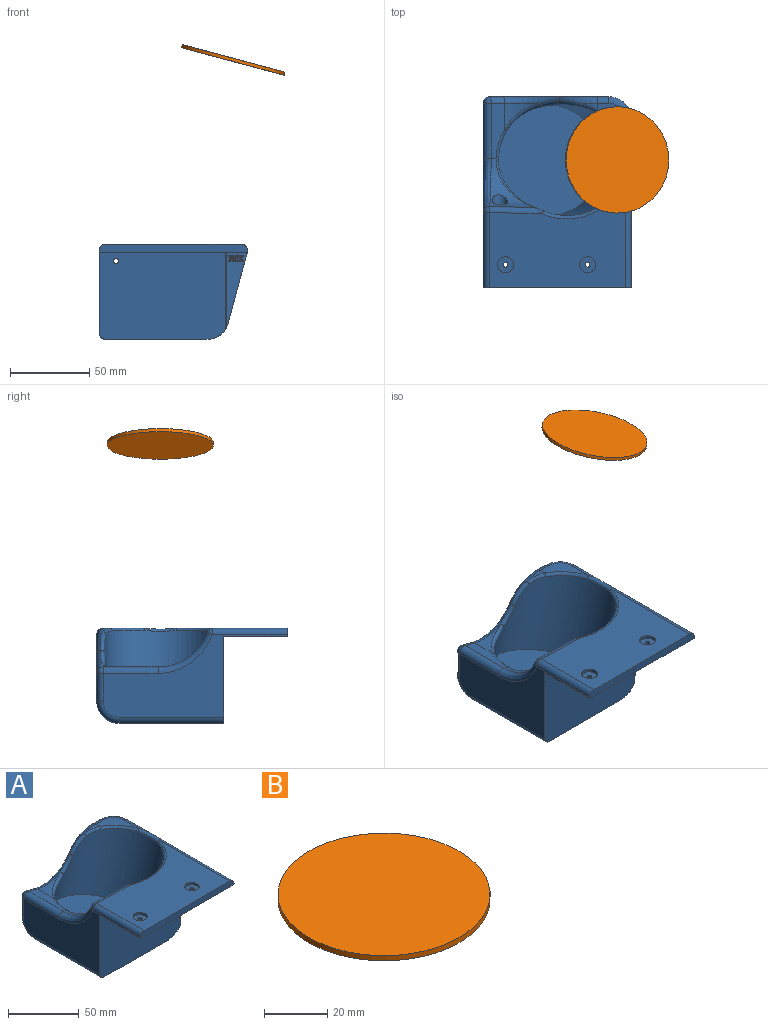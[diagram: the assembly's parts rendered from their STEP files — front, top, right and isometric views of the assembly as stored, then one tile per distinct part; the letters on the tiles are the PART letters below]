
ASSEMBLY  parts=2 mates=1
PART A: 290 faces, bbox 113.1x121.2x77.5 mm
  f0: plane 85.53x69.51mm, normal (0,0,1), area 3915.7mm2, adj f6,f20,f23,f265,f269,f278,f284
  f1: plane 48x13.37mm, normal (0.55,-0.83,0), area 362.4mm2, adj f110,f112,f113,f116,f117,f118,f119,f120
  f2: plane 79.97x54.9mm, normal (0,-1,0), area 4355.7mm2, adj f4,f8,f15,f109,f110,f264,f276
  f3: plane 75.17x42mm, normal (0,1,0), area 1714.4mm2, adj f25,f262,f267,f268,f270,f272,f275
  f4: plane 66x63.92mm, normal (0,0,-1), area 4218.6mm2, adj f2,f262,f264,f276
  f5: plane 25.51x17.47mm, normal (0,0,1), area 186.1mm2, adj f14,f265,f266,f267,f280
  f6: plane 93.52x5mm, normal (0,-1,0), area 460.7mm2, adj f0,f7,f8,f115,f265,f269
  f7: plane 93.32x48.76mm, normal (0,0,-1), area 3768.2mm2, adj f6,f8,f18,f21,f109,f111,f113,f115
  f8: plane 116x52.01mm, normal (-1,0,0), area 2518.3mm2, adj f2,f6,f7,f109,f269,f271,f273,f275
  f9: plane 70x67.62mm, normal (0.26,0,0.97), area 3848.5mm2, adj f10
  f10: cylinder r=35mm len=82.02mm, axis (0.26,0,0.97), area 7874.1mm2, adj f9,f280,f281,f282,f283,f284,f285,f286
  f11: plane 64.98x44.59mm, normal (0.97,0,-0.26), area 2815.9mm2, adj f25,f112,f114,f264,f265
  f12: plane 34.64x8.58mm, normal (0.26,0,0.97), area 240.8mm2, adj f13,f24,f272,f273,f289
  f13: cylinder r=30mm len=23.04mm, axis (0,-1,0), area 196.4mm2, adj f12,f270,f287
  f14: cylinder r=30mm len=11.81mm, axis (0,-1,0), area 24.4mm2, adj f5,f268,f281
  f15: cylinder r=1.5mm len=8mm, axis (0,1,0), area 75.4mm2, adj f2,f16
  f16: plane 10x10mm, normal (0,1,0), area 71.5mm2, adj f15,f17
  f17: cylinder r=5mm len=10mm, axis (0,1,0), area 215.5mm2, adj f16,f24
  f18: cylinder r=1.5mm len=3mm, axis (0,0,1), area 28.3mm2, adj f7,f19
  f19: plane 10x10mm, normal (0,0,1), area 71.5mm2, adj f18,f20
  f20: cylinder r=5mm len=10mm, axis (0,0,1), area 62.8mm2, adj f0,f19
  f21: cylinder r=1.5mm len=3mm, axis (0,0,1), area 28.3mm2, adj f7,f22
  f22: plane 10x10mm, normal (0,0,1), area 71.5mm2, adj f21,f23
  f23: cylinder r=5mm len=10mm, axis (0,0,1), area 62.8mm2, adj f0,f22
  f24: bspline ~58.91x32.85mm, area 466mm2, adj f12,f17,f271,f278,f288
  f25: cylinder r=14mm len=48.21mm, axis (-0.26,0,-0.97), area 985.7mm2, adj f3,f11,f263,f266
  f26: extruded ~0.82x0.61mm, area 0.6mm2, adj f27,f53,f108,f260
  f27: plane 0.75x0.5mm, normal (-0.83,-0.55,0), area 0.1mm2, adj f26,f28,f108,f261
  f28: extruded ~0.82x0.67mm, area 0.6mm2, adj f27,f29,f108,f259
  f29: extruded ~0.98x0.85mm, area 0.5mm2, adj f28,f30,f108,f257
  f30: extruded ~0.91x0.75mm, area 0.3mm2, adj f29,f31,f108,f255
  f31: extruded ~0.86x0.67mm, area 0.3mm2, adj f30,f32,f108,f253
  f32: plane 1.25x0.75mm, normal (0.83,0.55,0), area 1.1mm2, adj f31,f33,f108,f252
  f33: extruded ~0.87x0.67mm, area 0.3mm2, adj f32,f34,f108,f254
  f34: extruded ~0.92x0.75mm, area 0.3mm2, adj f33,f53,f108,f256
  f35: extruded ~0.85x0.72mm, area 0.4mm2, adj f36,f52,f232,f250
  f36: plane 0.7x0.49mm, normal (0.82,0.55,0.16), area 0.3mm2, adj f35,f37,f233,f251
  f37: plane 1.33x1.26mm, normal (0,0,1), area 0.9mm2, adj f36,f38,f231,f249
  f38: plane 0.67x0.48mm, normal (-0.83,-0.55,0), area 0.4mm2, adj f37,f39,f229,f247
  f39: plane 0.88x0.76mm, normal (-0.17,-0.12,-0.98), area 0.3mm2, adj f38,f40,f227,f245
  f40: plane 3.68x0.67mm, normal (-0.83,-0.55,0), area 2.9mm2, adj f39,f41,f225,f243
  f41: plane 1.46x1.34mm, normal (0,0,-1), area 1mm2, adj f40,f42,f223,f241
  f42: plane 0.67x0.48mm, normal (0.83,0.55,0), area 0.4mm2, adj f41,f43,f221,f239
  f43: plane 0.9x0.8mm, normal (0.16,0.1,0.98), area 0.3mm2, adj f42,f44,f219,f237
  f44: plane 1.05x0.67mm, normal (0.83,0.55,0), area 0.8mm2, adj f43,f45,f217,f235
  f45: extruded ~0.84x0.7mm, area 0.3mm2, adj f44,f46,f216,f234
  f46: extruded ~0.89x0.77mm, area 0.3mm2, adj f45,f47,f218,f236
  f47: extruded ~1.15x1.14mm, area 0.8mm2, adj f46,f48,f220,f238
  f48: extruded ~1.12x0.83mm, area 0.9mm2, adj f47,f49,f222,f240
  f49: plane 0.67x0.44mm, normal (0.83,0.55,0), area 0mm2, adj f48,f50,f224,f242
  f50: extruded ~1.05x0.83mm, area 0.9mm2, adj f49,f51,f226,f244
  f51: extruded ~1.14x1.13mm, area 0.8mm2, adj f50,f52,f228,f246
  f52: extruded ~0.9x0.8mm, area 0.4mm2, adj f35,f51,f230,f248
  f53: extruded ~0.98x0.85mm, area 0.5mm2, adj f26,f34,f108,f258
  f54: plane 4.09x2.35mm, normal (0.55,-0.83,0), area 4.9mm2, adj f234,f235,f236,f237,f238,f239,f240,f241
  f55: plane 0.67x0.48mm, normal (-0.83,-0.55,0), area 0.4mm2, adj f56,f76,f189,f211
  f56: plane 1.8x1.57mm, normal (0,0,-1), area 1.3mm2, adj f55,f57,f187,f209
  f57: plane 0.67x0.48mm, normal (0.83,0.55,0), area 0.4mm2, adj f56,f58,f185,f207
  f58: plane 0.9x0.8mm, normal (0.16,0.11,0.98), area 0.3mm2, adj f57,f59,f183,f205
  f59: plane 2.1x0.67mm, normal (0.83,0.55,0), area 1.7mm2, adj f58,f60,f181,f203
  f60: plane 0.7x0.47mm, normal (0.13,0.09,-0.99), area 0mm2, adj f59,f61,f179,f181,f201
  f61: plane 2.66x1.77mm, normal (-0.71,-0.48,-0.51), area 2.5mm2, adj f60,f62,f179,f199
  f62: plane 1.45x1.34mm, normal (0,0,-1), area 1mm2, adj f61,f63,f177,f197
  f63: plane 0.67x0.48mm, normal (0.83,0.55,0), area 0.4mm2, adj f62,f64,f175,f195
  f64: plane 0.9x0.79mm, normal (0.16,0.11,0.98), area 0.3mm2, adj f63,f65,f174,f194
  f65: plane 2.83x0.67mm, normal (0.83,0.55,0), area 2.3mm2, adj f64,f66,f176,f196
  f66: plane 0.9x0.79mm, normal (0.16,0.11,-0.98), area 0.3mm2, adj f65,f67,f178,f198
  f67: plane 0.67x0.48mm, normal (0.83,0.55,0), area 0.4mm2, adj f66,f68,f180,f200
  f68: plane 1.8x1.57mm, normal (0,0,1), area 1.3mm2, adj f67,f69,f182,f202
  f69: plane 0.67x0.48mm, normal (-0.83,-0.55,0), area 0.4mm2, adj f68,f70,f184,f204
  f70: plane 0.9x0.8mm, normal (-0.16,-0.11,-0.98), area 0.3mm2, adj f69,f71,f186,f206
  f71: plane 2.1x0.67mm, normal (-0.83,-0.55,0), area 1.7mm2, adj f70,f72,f188,f208
  f72: plane 0.7x0.47mm, normal (-0.17,-0.11,0.98), area 0mm2, adj f71,f73,f188,f190,f210
  f73: plane 2.66x1.77mm, normal (0.71,0.48,0.51), area 2.5mm2, adj f72,f74,f190,f212
  f74: plane 1.1x1.1mm, normal (0,0,1), area 0.6mm2, adj f73,f75,f192,f214
  f75: plane 3.39x0.67mm, normal (-0.83,-0.55,0), area 2.7mm2, adj f74,f76,f193,f215
  f76: plane 0.9x0.8mm, normal (-0.16,-0.11,0.98), area 0.3mm2, adj f55,f75,f191,f213
  f77: plane 3.75x3.19mm, normal (0.55,-0.83,0), area 6.8mm2, adj f194,f195,f196,f197,f198,f199,f200,f201
  f78: plane 0.9x0.79mm, normal (0.16,0.11,-0.98), area 0.3mm2, adj f79,f106,f143,f172
  f79: plane 0.67x0.48mm, normal (0.83,0.55,0), area 0.4mm2, adj f78,f80,f144,f173
  f80: plane 1.79x1.56mm, normal (0,0,1), area 1.3mm2, adj f79,f81,f142,f171
  f81: plane 0.67x0.48mm, normal (-0.83,-0.55,0), area 0.4mm2, adj f80,f82,f140,f169
  f82: plane 0.89x0.78mm, normal (-0.17,-0.11,-0.98), area 0.3mm2, adj f81,f83,f138,f167
  f83: plane 1.09x0.67mm, normal (-0.83,-0.55,0), area 0.9mm2, adj f82,f84,f136,f165
  f84: plane 0.91x0.81mm, normal (0,0,1), area 0.4mm2, adj f83,f85,f134,f163
  f85: plane 1.14x1.09mm, normal (0.69,0.46,0.55), area 1.1mm2, adj f84,f86,f132,f161
  f86: plane 0.8x0.65mm, normal (0.11,0.07,-0.99), area 0.2mm2, adj f85,f87,f130,f159
  f87: plane 0.67x0.48mm, normal (0.83,0.55,0), area 0.4mm2, adj f86,f88,f128,f157
  f88: plane 1.75x1.53mm, normal (0,0,1), area 1.3mm2, adj f87,f89,f126,f155
  f89: plane 0.67x0.48mm, normal (-0.83,-0.55,0), area 0.4mm2, adj f88,f90,f124,f153
  f90: plane 0.89x0.77mm, normal (-0.14,-0.09,-0.99), area 0.3mm2, adj f89,f91,f122,f151
  f91: plane 1.56x1.35mm, normal (-0.68,-0.45,-0.57), area 1.5mm2, adj f90,f92,f120,f149
  f92: plane 1.3x1.25mm, normal (-0.67,-0.44,0.6), area 1.3mm2, adj f91,f93,f118,f147
  f93: plane 0.9x0.8mm, normal (-0.14,-0.09,0.99), area 0.3mm2, adj f92,f94,f116,f145
  f94: plane 0.67x0.48mm, normal (-0.83,-0.55,0), area 0.4mm2, adj f93,f95,f117,f146
  f95: plane 1.75x1.53mm, normal (0,0,-1), area 1.3mm2, adj f94,f96,f119,f148
  f96: plane 0.67x0.48mm, normal (0.83,0.55,0), area 0.4mm2, adj f95,f97,f121,f150
  f97: plane 0.8x0.64mm, normal (0.11,0.08,0.99), area 0.2mm2, adj f96,f98,f123,f152
  f98: plane 1.1x1.09mm, normal (0.69,0.46,-0.57), area 1.1mm2, adj f97,f99,f125,f154
  f99: plane 0.86x0.73mm, normal (0,0,-1), area 0.3mm2, adj f98,f100,f127,f156
  f100: plane 1.05x0.67mm, normal (-0.83,-0.55,0), area 0.8mm2, adj f99,f101,f129,f158
  f101: plane 0.89x0.78mm, normal (-0.17,-0.11,0.98), area 0.3mm2, adj f100,f102,f131,f160
  f102: plane 0.67x0.48mm, normal (-0.83,-0.55,0), area 0.4mm2, adj f101,f103,f133,f162
  f103: plane 1.79x1.56mm, normal (0,0,-1), area 1.3mm2, adj f102,f104,f135,f164
  f104: plane 0.67x0.48mm, normal (0.83,0.55,0), area 0.4mm2, adj f103,f105,f137,f166
  f105: plane 0.9x0.79mm, normal (0.16,0.11,0.98), area 0.3mm2, adj f104,f106,f139,f168
  f106: plane 2.83x0.67mm, normal (0.83,0.55,0), area 2.3mm2, adj f78,f105,f141,f170
  f107: plane 3.75x2.94mm, normal (0.55,-0.83,0), area 5.9mm2, adj f145,f146,f147,f148,f149,f150,f151,f152
  f108: plane 1.81x0.88mm, normal (0.55,-0.83,0), area 1.7mm2, adj f26,f27,f28,f29,f30,f31,f32,f33
  f109: cylinder r=0.1mm len=79.97mm, axis (-1,0,0), area 12.6mm2, adj f2,f7,f8,f111
  f110: cylinder r=0.1mm len=48.02mm, axis (0,0,1), area 2.8mm2, adj f1,f2,f111,f264
  f111: torus R=0.2mm, axis (0,0,-1), area 0mm2, adj f7,f109,f110,f113
  f112: cylinder r=0.1mm len=45.64mm, axis (-0.26,-0.17,-0.95), area 4.8mm2, adj f1,f11,f114,f264
  f113: cylinder r=0.1mm len=13.35mm, axis (-0.83,-0.55,0), area 2.5mm2, adj f1,f7,f111,f114
  f114: bspline ~0.23x0.22mm, area 0mm2, adj f11,f112,f113,f115,f265
  f115: cylinder r=0.1mm len=48.76mm, axis (0,-1,0), area 5.6mm2, adj f6,f7,f114,f265
  f116: cylinder r=0.1mm len=0.5mm, axis (-0.82,-0.55,-0.17), area 0.1mm2, adj f1,f93,f117,f118
  f117: cylinder r=0.1mm len=0.66mm, axis (0,0,-1), area 0.1mm2, adj f1,f94,f116,f119
  f118: cylinder r=0.1mm len=1.36mm, axis (-0.5,-0.33,-0.8), area 0.2mm2, adj f1,f92,f116,f120
  f119: cylinder r=0.1mm len=1.52mm, axis (0.83,0.55,0), area 0.3mm2, adj f1,f95,f117,f121
  f120: cylinder r=0.1mm len=1.62mm, axis (0.48,0.32,-0.82), area 0.3mm2, adj f1,f91,f118,f122
  f121: cylinder r=0.1mm len=0.66mm, axis (0,0,1), area 0.1mm2, adj f1,f96,f119,f123
  f122: cylinder r=0.1mm len=0.47mm, axis (0.82,0.55,-0.17), area 0.1mm2, adj f1,f90,f120,f124
  f123: cylinder r=0.1mm len=0.31mm, axis (-0.82,-0.55,0.14), area 0mm2, adj f1,f97,f121,f125
  f124: cylinder r=0.1mm len=0.66mm, axis (0,0,-1), area 0.1mm2, adj f1,f89,f122,f126
  f125: cylinder r=0.1mm len=1.16mm, axis (0.47,0.31,0.82), area 0.2mm2, adj f1,f98,f123,f127
  f126: cylinder r=0.1mm len=1.52mm, axis (-0.83,-0.55,0), area 0.3mm2, adj f1,f88,f124,f128
  f127: cylinder r=0.1mm len=0.34mm, axis (0.83,0.55,0), area 0mm2, adj f1,f99,f125,f129
  f128: cylinder r=0.1mm len=0.66mm, axis (0,0,1), area 0.1mm2, adj f1,f87,f126,f130
  f129: cylinder r=0.1mm len=1.05mm, axis (0,0,-1), area 0.2mm2, adj f1,f100,f127,f131
  f130: cylinder r=0.1mm len=0.32mm, axis (0.82,0.55,0.13), area 0mm2, adj f1,f86,f128,f132
  f131: cylinder r=0.1mm len=0.47mm, axis (-0.82,-0.54,-0.2), area 0.1mm2, adj f1,f101,f129,f133
  f132: cylinder r=0.1mm len=1.2mm, axis (-0.46,-0.31,0.83), area 0.2mm2, adj f1,f85,f130,f134
  f133: cylinder r=0.1mm len=0.66mm, axis (0,0,-1), area 0.1mm2, adj f1,f102,f131,f135
  f134: cylinder r=0.1mm len=0.42mm, axis (-0.83,-0.55,0), area 0.1mm2, adj f1,f84,f132,f136
  f135: cylinder r=0.1mm len=1.56mm, axis (0.83,0.55,0), area 0.3mm2, adj f1,f103,f133,f137
  f136: cylinder r=0.1mm len=1.09mm, axis (0,0,-1), area 0.2mm2, adj f1,f83,f134,f138
  f137: cylinder r=0.1mm len=0.66mm, axis (0,0,1), area 0.1mm2, adj f1,f104,f135,f139
  f138: cylinder r=0.1mm len=0.47mm, axis (0.82,0.54,-0.2), area 0.1mm2, adj f1,f82,f136,f140
  f139: cylinder r=0.1mm len=0.46mm, axis (-0.82,-0.54,0.19), area 0.1mm2, adj f1,f105,f137,f141
  f140: cylinder r=0.1mm len=0.66mm, axis (0,0,-1), area 0.1mm2, adj f1,f81,f138,f142
  f141: cylinder r=0.1mm len=2.83mm, axis (0,0,1), area 0.4mm2, adj f1,f106,f139,f143
  f142: cylinder r=0.1mm len=1.56mm, axis (-0.83,-0.55,0), area 0.3mm2, adj f1,f80,f140,f144
  f143: cylinder r=0.1mm len=0.46mm, axis (0.82,0.54,0.19), area 0.1mm2, adj f1,f78,f141,f144
  f144: cylinder r=0.1mm len=0.66mm, axis (0,0,1), area 0.1mm2, adj f1,f79,f142,f143
  f145: cylinder r=0.1mm len=0.46mm, axis (0.82,0.55,0.17), area 0.1mm2, adj f93,f107,f146,f147
  f146: cylinder r=0.1mm len=0.48mm, axis (0,0,1), area 0.1mm2, adj f94,f107,f145,f148
  f147: cylinder r=0.1mm len=1.45mm, axis (0.5,0.33,0.8), area 0.3mm2, adj f92,f107,f145,f149
  f148: cylinder r=0.1mm len=1.36mm, axis (-0.83,-0.55,0), area 0.2mm2, adj f95,f107,f146,f150
  f149: cylinder r=0.1mm len=1.71mm, axis (-0.48,-0.32,0.82), area 0.3mm2, adj f91,f107,f147,f151
  f150: cylinder r=0.1mm len=0.48mm, axis (0,0,-1), area 0.1mm2, adj f96,f107,f148,f152
  f151: cylinder r=0.1mm len=0.43mm, axis (-0.82,-0.55,0.17), area 0.1mm2, adj f90,f107,f149,f153
  f152: cylinder r=0.1mm len=0.37mm, axis (0.82,0.55,-0.14), area 0mm2, adj f97,f107,f150,f154
  f153: cylinder r=0.1mm len=0.48mm, axis (0,0,1), area 0.1mm2, adj f89,f107,f151,f155
  f154: cylinder r=0.1mm len=1.34mm, axis (-0.47,-0.31,-0.82), area 0.2mm2, adj f98,f107,f152,f156
  f155: cylinder r=0.1mm len=1.36mm, axis (0.83,0.55,0), area 0.2mm2, adj f88,f107,f153,f157
  f156: cylinder r=0.1mm len=0.47mm, axis (-0.83,-0.55,0), area 0.1mm2, adj f99,f107,f154,f158
  f157: cylinder r=0.1mm len=0.48mm, axis (0,0,-1), area 0.1mm2, adj f87,f107,f155,f159
  f158: cylinder r=0.1mm len=1.24mm, axis (0,0,1), area 0.2mm2, adj f100,f107,f156,f160
  f159: cylinder r=0.1mm len=0.38mm, axis (-0.82,-0.55,-0.13), area 0mm2, adj f86,f107,f157,f161
  f160: cylinder r=0.1mm len=0.47mm, axis (0.82,0.54,0.2), area 0.1mm2, adj f101,f107,f158,f162
  f161: cylinder r=0.1mm len=1.38mm, axis (0.46,0.31,-0.83), area 0.2mm2, adj f85,f107,f159,f163
  f162: cylinder r=0.1mm len=0.48mm, axis (0,0,1), area 0.1mm2, adj f102,f107,f160,f164
  f163: cylinder r=0.1mm len=0.55mm, axis (0.83,0.55,0), area 0.1mm2, adj f84,f107,f161,f165
  f164: cylinder r=0.1mm len=1.4mm, axis (-0.83,-0.55,0), area 0.2mm2, adj f103,f107,f162,f166
  f165: cylinder r=0.1mm len=1.27mm, axis (0,0,1), area 0.2mm2, adj f83,f107,f163,f167
  f166: cylinder r=0.1mm len=0.48mm, axis (0,0,-1), area 0.1mm2, adj f104,f107,f164,f168
  f167: cylinder r=0.1mm len=0.47mm, axis (-0.82,-0.54,0.2), area 0.1mm2, adj f82,f107,f165,f169
  f168: cylinder r=0.1mm len=0.46mm, axis (0.82,0.54,-0.19), area 0.1mm2, adj f105,f107,f166,f170
  f169: cylinder r=0.1mm len=0.48mm, axis (0,0,1), area 0.1mm2, adj f81,f107,f167,f171
  f170: cylinder r=0.1mm len=3mm, axis (0,0,-1), area 0.5mm2, adj f106,f107,f168,f172
  f171: cylinder r=0.1mm len=1.4mm, axis (0.83,0.55,0), area 0.2mm2, adj f80,f107,f169,f173
  f172: cylinder r=0.1mm len=0.46mm, axis (-0.82,-0.54,-0.19), area 0.1mm2, adj f78,f107,f170,f173
  f173: cylinder r=0.1mm len=0.48mm, axis (0,0,-1), area 0.1mm2, adj f79,f107,f171,f172
  f174: cylinder r=0.1mm len=0.46mm, axis (-0.82,-0.54,0.19), area 0.1mm2, adj f1,f64,f175,f176
  f175: cylinder r=0.1mm len=0.66mm, axis (0,0,1), area 0.1mm2, adj f1,f63,f174,f177
  f176: cylinder r=0.1mm len=2.83mm, axis (0,0,1), area 0.4mm2, adj f1,f65,f174,f178
  f177: cylinder r=0.1mm len=1.19mm, axis (0.83,0.55,0), area 0.2mm2, adj f1,f62,f175,f179
  f178: cylinder r=0.1mm len=0.46mm, axis (0.82,0.54,0.19), area 0.1mm2, adj f1,f66,f176,f180
  f179: cylinder r=0.1mm len=2.76mm, axis (0.43,0.29,-0.86), area 0.5mm2, adj f1,f60,f61,f177,f181
  f180: cylinder r=0.1mm len=0.66mm, axis (0,0,1), area 0.1mm2, adj f1,f67,f178,f182
  f181: cylinder r=0.1mm len=2.1mm, axis (0,0,1), area 0.3mm2, adj f1,f59,f60,f179,f183
  f182: cylinder r=0.1mm len=1.58mm, axis (-0.83,-0.55,0), area 0.3mm2, adj f1,f68,f180,f184
  f183: cylinder r=0.1mm len=0.46mm, axis (-0.82,-0.54,0.19), area 0.1mm2, adj f1,f58,f181,f185
  f184: cylinder r=0.1mm len=0.66mm, axis (0,0,-1), area 0.1mm2, adj f1,f69,f182,f186
  f185: cylinder r=0.1mm len=0.66mm, axis (0,0,1), area 0.1mm2, adj f1,f57,f183,f187
  f186: cylinder r=0.1mm len=0.49mm, axis (0.82,0.54,-0.19), area 0.1mm2, adj f1,f70,f184,f188
  f187: cylinder r=0.1mm len=1.58mm, axis (0.83,0.55,0), area 0.3mm2, adj f1,f56,f185,f189
  f188: cylinder r=0.1mm len=2.1mm, axis (0,0,-1), area 0.3mm2, adj f1,f71,f72,f186,f190
  f189: cylinder r=0.1mm len=0.66mm, axis (0,0,-1), area 0.1mm2, adj f1,f55,f187,f191
  f190: cylinder r=0.1mm len=2.76mm, axis (-0.43,-0.29,0.86), area 0.5mm2, adj f1,f72,f73,f188,f192
  f191: cylinder r=0.1mm len=0.49mm, axis (-0.82,-0.54,-0.19), area 0.1mm2, adj f1,f76,f189,f193
  f192: cylinder r=0.1mm len=0.84mm, axis (-0.83,-0.55,0), area 0.1mm2, adj f1,f74,f190,f193
  f193: cylinder r=0.1mm len=3.49mm, axis (0,0,-1), area 0.5mm2, adj f1,f75,f191,f192
  f194: cylinder r=0.1mm len=0.46mm, axis (0.82,0.54,-0.19), area 0.1mm2, adj f64,f77,f195,f196
  f195: cylinder r=0.1mm len=0.48mm, axis (0,0,-1), area 0.1mm2, adj f63,f77,f194,f197
  f196: cylinder r=0.1mm len=3mm, axis (0,0,-1), area 0.5mm2, adj f65,f77,f194,f198
  f197: cylinder r=0.1mm len=1.06mm, axis (-0.83,-0.55,0), area 0.2mm2, adj f62,f77,f195,f199
  f198: cylinder r=0.1mm len=0.46mm, axis (-0.82,-0.54,-0.19), area 0.1mm2, adj f66,f77,f196,f200
  f199: cylinder r=0.1mm len=2.77mm, axis (-0.43,-0.29,0.86), area 0.5mm2, adj f61,f77,f197,f201
  f200: cylinder r=0.1mm len=0.48mm, axis (0,0,-1), area 0.1mm2, adj f67,f77,f198,f202
  f201: cylinder r=0.1mm len=0.18mm, axis (-0.82,-0.55,-0.16), area 0mm2, adj f60,f77,f199,f203
  f202: cylinder r=0.1mm len=1.42mm, axis (0.83,0.55,0), area 0.2mm2, adj f68,f77,f200,f204
  f203: cylinder r=0.1mm len=2.26mm, axis (0,0,-1), area 0.3mm2, adj f59,f77,f201,f205
  f204: cylinder r=0.1mm len=0.48mm, axis (0,0,1), area 0.1mm2, adj f69,f77,f202,f206
  f205: cylinder r=0.1mm len=0.46mm, axis (0.82,0.54,-0.19), area 0.1mm2, adj f58,f77,f203,f207
  f206: cylinder r=0.1mm len=0.49mm, axis (-0.82,-0.54,0.19), area 0.1mm2, adj f70,f77,f204,f208
  f207: cylinder r=0.1mm len=0.48mm, axis (0,0,-1), area 0.1mm2, adj f57,f77,f205,f209
  f208: cylinder r=0.1mm len=2.26mm, axis (0,0,1), area 0.3mm2, adj f71,f77,f206,f210
  f209: cylinder r=0.1mm len=1.42mm, axis (-0.83,-0.55,0), area 0.2mm2, adj f56,f77,f207,f211
  f210: cylinder r=0.1mm len=0.21mm, axis (0.81,0.54,0.21), area 0mm2, adj f72,f77,f208,f212
  f211: cylinder r=0.1mm len=0.48mm, axis (0,0,1), area 0.1mm2, adj f55,f77,f209,f213
  f212: cylinder r=0.1mm len=2.77mm, axis (0.43,0.29,-0.86), area 0.5mm2, adj f73,f77,f210,f214
  f213: cylinder r=0.1mm len=0.49mm, axis (0.82,0.54,0.19), area 0.1mm2, adj f76,f77,f211,f215
  f214: cylinder r=0.1mm len=0.71mm, axis (0.83,0.55,0), area 0.1mm2, adj f74,f77,f212,f215
  f215: cylinder r=0.1mm len=3.47mm, axis (0,0,1), area 0.5mm2, adj f75,f77,f213,f214
  f216: bspline ~0.51x0.5mm, area 0mm2, adj f1,f45,f217,f218
  f217: cylinder r=0.1mm len=1.05mm, axis (0,0,1), area 0.1mm2, adj f1,f44,f216,f219
  f218: bspline ~0.5x0.35mm, area 0.1mm2, adj f1,f46,f216,f220
  f219: cylinder r=0.1mm len=0.46mm, axis (-0.82,-0.54,0.19), area 0.1mm2, adj f1,f43,f217,f221
  f220: bspline ~1.13x0.84mm, area 0.2mm2, adj f1,f47,f218,f222
  f221: cylinder r=0.1mm len=0.66mm, axis (0,0,1), area 0.1mm2, adj f1,f42,f219,f223
  f222: bspline ~1.62x0.45mm, area 0.2mm2, adj f1,f48,f220,f224
  f223: cylinder r=0.1mm len=1.23mm, axis (0.83,0.55,0), area 0.2mm2, adj f1,f41,f221,f225
  f224: cylinder r=0.1mm len=0.14mm, axis (0,0,1), area 0mm2, adj f1,f49,f222,f226
  f225: cylinder r=0.1mm len=3.78mm, axis (0,0,-1), area 0.6mm2, adj f1,f40,f223,f227
  f226: bspline ~1.38x0.36mm, area 0.2mm2, adj f1,f50,f224,f228
  f227: cylinder r=0.1mm len=0.46mm, axis (0.81,0.54,-0.21), area 0.1mm2, adj f1,f39,f225,f229
  f228: bspline ~0.97x0.73mm, area 0.2mm2, adj f1,f51,f226,f230
  f229: cylinder r=0.1mm len=0.66mm, axis (0,0,-1), area 0.1mm2, adj f1,f38,f227,f231
  f230: bspline ~0.55x0.38mm, area 0.1mm2, adj f1,f52,f228,f232
  f231: cylinder r=0.1mm len=1.1mm, axis (-0.83,-0.55,0), area 0.2mm2, adj f1,f37,f229,f233
  f232: bspline ~0.56x0.54mm, area 0.1mm2, adj f1,f35,f230,f233
  f233: cylinder r=0.1mm len=0.46mm, axis (-0.14,-0.09,0.99), area 0mm2, adj f1,f36,f231,f232
  f234: bspline ~0.73x0.65mm, area 0.1mm2, adj f45,f54,f235,f236
  f235: cylinder r=0.1mm len=1.43mm, axis (0,0,-1), area 0.2mm2, adj f44,f54,f234,f237
  f236: bspline ~0.46x0.36mm, area 0.1mm2, adj f46,f54,f234,f238
  f237: cylinder r=0.1mm len=0.46mm, axis (0.82,0.54,-0.19), area 0.1mm2, adj f43,f54,f235,f239
  f238: bspline ~1.02x0.73mm, area 0.1mm2, adj f47,f54,f236,f240
  f239: cylinder r=0.1mm len=0.48mm, axis (0,0,-1), area 0.1mm2, adj f42,f54,f237,f241
  f240: bspline ~1.56x0.44mm, area 0.2mm2, adj f48,f54,f238,f242
  f241: cylinder r=0.1mm len=1.07mm, axis (-0.83,-0.55,0), area 0.2mm2, adj f41,f54,f239,f243
  f242: cylinder r=0.1mm len=0.14mm, axis (0,0,-1), area 0mm2, adj f49,f54,f240,f244
  f243: cylinder r=0.1mm len=3.76mm, axis (0,0,1), area 0.6mm2, adj f40,f54,f241,f245
  f244: bspline ~1.33x0.34mm, area 0.2mm2, adj f50,f54,f242,f246
  f245: cylinder r=0.1mm len=0.46mm, axis (-0.81,-0.54,0.21), area 0.1mm2, adj f39,f54,f243,f247
  f246: bspline ~0.96x0.68mm, area 0.1mm2, adj f51,f54,f244,f248
  f247: cylinder r=0.1mm len=0.48mm, axis (0,0,1), area 0.1mm2, adj f38,f54,f245,f249
  f248: bspline ~0.51x0.38mm, area 0.1mm2, adj f52,f54,f246,f250
  f249: cylinder r=0.1mm len=0.94mm, axis (0.83,0.55,0), area 0.2mm2, adj f37,f54,f247,f251
  f250: bspline ~0.72x0.62mm, area 0.1mm2, adj f35,f54,f248,f251
  f251: cylinder r=0.1mm len=0.62mm, axis (0.14,0.09,-0.99), area 0.1mm2, adj f36,f54,f249,f250
  f252: cylinder r=0.1mm len=1.3mm, axis (0,0,-1), area 0.2mm2, adj f32,f54,f253,f254
  f253: bspline ~0.42x0.34mm, area 0.1mm2, adj f31,f54,f252,f255
  f254: bspline ~0.56x0.42mm, area 0.1mm2, adj f33,f54,f252,f256
  f255: bspline ~0.37x0.32mm, area 0.1mm2, adj f30,f54,f253,f257
  f256: bspline ~0.37x0.32mm, area 0.1mm2, adj f34,f54,f254,f258
  f257: bspline ~0.54x0.45mm, area 0.1mm2, adj f29,f54,f255,f259
  f258: bspline ~0.58x0.38mm, area 0.1mm2, adj f53,f54,f256,f260
  f259: bspline ~0.9x0.26mm, area 0.1mm2, adj f28,f54,f257,f261
  f260: bspline ~0.81x0.3mm, area 0.1mm2, adj f26,f54,f258,f261
  f261: cylinder r=0.1mm len=0.14mm, axis (0,0,1), area 0mm2, adj f27,f54,f259,f260
  f262: cylinder r=14mm len=63.92mm, axis (-1,0,0), area 1405.6mm2, adj f3,f4,f263,f277
  f263: sphere r=14mm, area 379.7mm2, adj f25,f262,f264
  f264: cylinder r=14mm len=66mm, axis (0,-1,0), area 1207.6mm2, adj f1,f2,f4,f11,f110,f112,f263
  f265: cylinder r=4mm len=106mm, axis (0,-1,0), area 728.7mm2, adj f0,f5,f6,f11,f114,f115,f266,f282
  f266: bspline ~18.04x14.73mm, area 140.3mm2, adj f5,f25,f265,f267
  f267: cylinder r=4mm len=7.12mm, axis (-1,0,0), area 44.7mm2, adj f3,f5,f266,f268
  f268: torus R=26mm, axis (0,1,0), area 152.3mm2, adj f3,f14,f267,f270,f283
  f269: cylinder r=4mm len=47.11mm, axis (0,-1,0), area 296mm2, adj f0,f6,f8,f279
  f270: torus R=34mm, axis (0,1,0), area 235.8mm2, adj f3,f13,f268,f272,f285
  f271: bspline ~35.66x26.86mm, area 288.5mm2, adj f8,f24,f273,f279
  f272: cylinder r=4mm len=9.61mm, axis (-0.97,0,0.26), area 55.8mm2, adj f3,f12,f270,f274
  f273: cylinder r=4mm len=34.64mm, axis (0,-1,0), area 253.9mm2, adj f8,f12,f271,f274
  f274: sphere r=4mm, area 21.5mm2, adj f272,f273,f275
  f275: cylinder r=4mm len=17.58mm, axis (0,0,1), area 110.4mm2, adj f3,f8,f274,f277
  f276: cylinder r=4mm len=66mm, axis (0,1,0), area 414.7mm2, adj f2,f4,f8,f277
  f277: torus R=10mm, axis (1,0,0), area 123.8mm2, adj f8,f262,f275,f276
  f278: bspline ~57.7x5.02mm, area 164.9mm2, adj f0,f24,f279,f286
  f279: sphere r=4mm, area 21mm2, adj f269,f271,f278
  f280: bspline ~22.06x18.44mm, area 75.4mm2, adj f5,f10,f281,f282
  f281: bspline ~16.09x7.66mm, area 34.6mm2, adj f10,f14,f280,f283
  f282: bspline ~22.37x4.89mm, area 75.9mm2, adj f10,f265,f280,f284
  f283: bspline ~17.57x15.56mm, area 66.2mm2, adj f10,f268,f281,f285
  f284: bspline ~52.32x27.08mm, area 184.3mm2, adj f0,f10,f282,f286
  f285: bspline ~15.53x15.38mm, area 58.3mm2, adj f10,f270,f283,f287
  f286: bspline ~6.97x5.14mm, area 14.5mm2, adj f10,f278,f284,f288
  f287: bspline ~26.44x18.61mm, area 101.3mm2, adj f10,f13,f285,f289
  f288: bspline ~34.72x26.18mm, area 113.8mm2, adj f10,f24,f286,f289
  f289: torus R=37mm, axis (0.26,0,0.97), area 57.9mm2, adj f10,f12,f287,f288
PART B: 3 faces, bbox 67x67x2 mm
  f0: cylinder r=33.5mm len=67mm, axis (0,0,-1), area 421mm2, adj f1,f2
  f1: plane 67x67mm, normal (0,0,1), area 3525.7mm2, adj f0
  f2: plane 67x67mm, normal (0,0,-1), area 3525.7mm2, adj f0
PLACE A t=(19.93,-83.1,34.62)mm fixed
PLACE B rot(axis=(0,1,0),15deg) t=(144.05,-79.16,144.14)mm
MATE slider B.f0 <-> A.f289  axis (-0.26,0,-0.97) through (104.39,-53.1,155.8)mm
